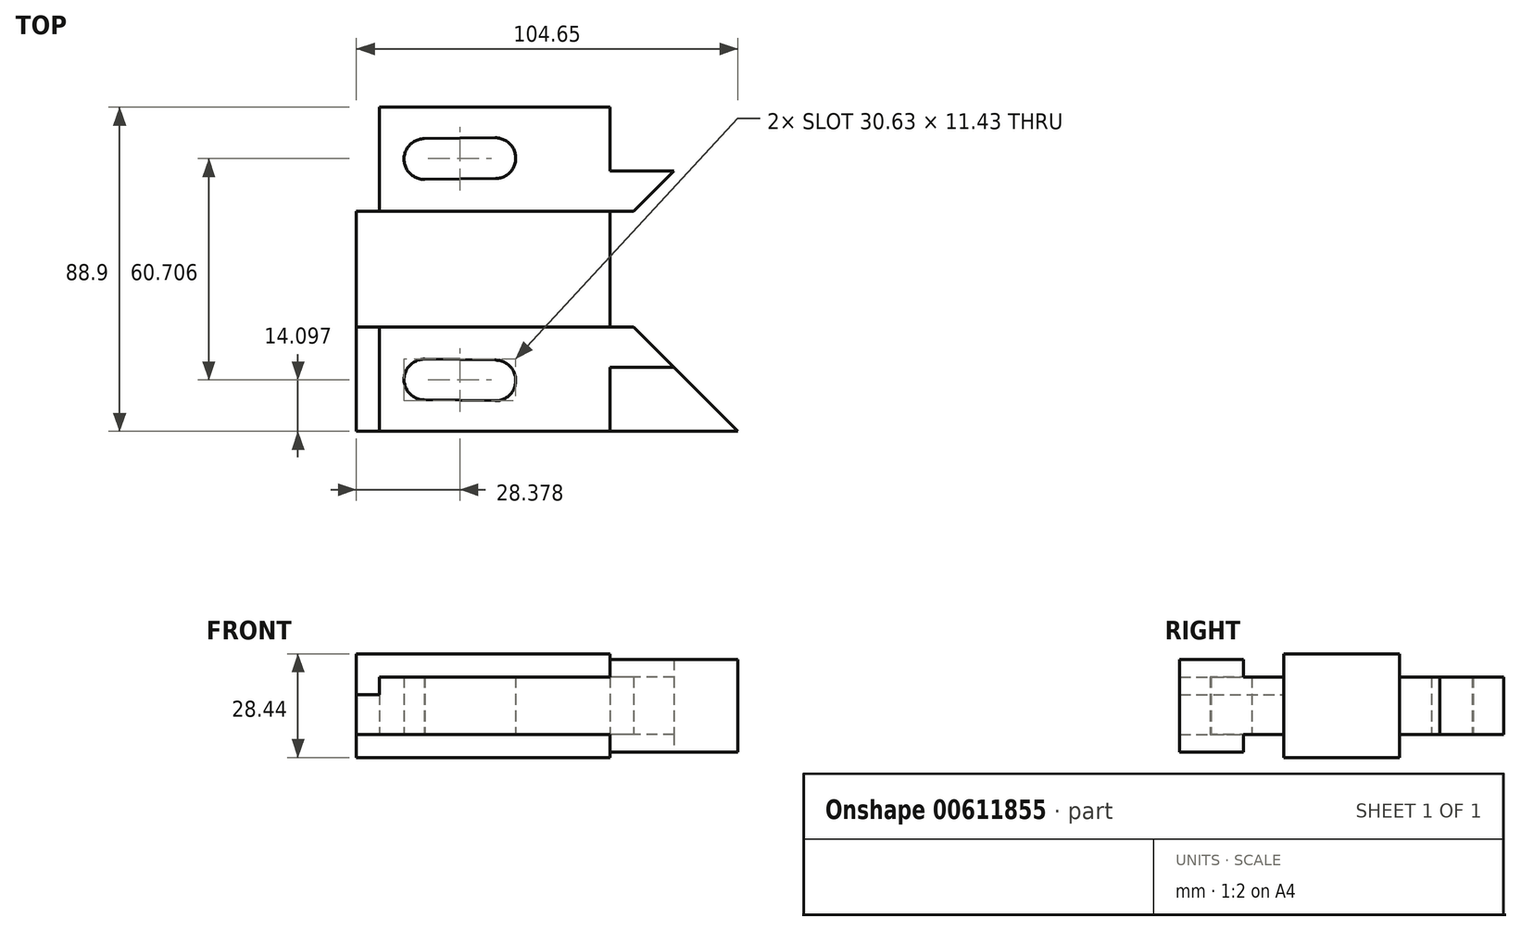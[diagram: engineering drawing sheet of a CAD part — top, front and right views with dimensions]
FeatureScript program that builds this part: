
annotation { "Feature Type Name" : "Feature", "Feature Type Description" : "" }
export const myFeature = defineFeature(function(context is Context, id is Id, definition is map)
    precondition{}
    {
        {
            var Q0;
            Q0=qCreatedBy(makeId("Top.planeOp"),FACE);
            var sketch = newSketch(context, id + "F0", { "sketchPlane" : qUnion([Q0])});
            skLineSegment(sketch, "E0.top", {"start": v(0, 15.88) * mm, "end": v(-69.6, 15.88) * mm});
            skLineSegment(sketch, "E0.left", {"start": v(0, 0) * mm, "end": v(0, 15.88) * mm});
            skLineSegment(sketch, "E0.right", {"start": v(-69.6, 0) * mm, "end": v(-69.6, 15.88) * mm});
            skLineSegment(sketch, "E1.bottom", {"start": v(-69.6, 15.88) * mm, "end": v(-50.95, 15.88) * mm});
            skLineSegment(sketch, "E1.top", {"start": v(-69.6, 44.45) * mm, "end": v(35.05, 44.45) * mm});
            skLineSegment(sketch, "E1.left", {"start": v(-69.6, 15.88) * mm, "end": v(-69.6, 44.45) * mm});
            skLineSegment(sketch, "E2.bottom", {"start": v(-69.6, 44.45) * mm, "end": v(-63.25, 44.45) * mm});
            skLineSegment(sketch, "E2.top", {"start": v(-69.6, 15.88) * mm, "end": v(-63.25, 15.88) * mm});
            skLineSegment(sketch, "E2.left", {"start": v(-69.6, 44.45) * mm, "end": v(-69.6, 15.88) * mm});
            skLineSegment(sketch, "E2.right", {"start": v(-63.25, 44.45) * mm, "end": v(-63.25, 15.88) * mm});
            skLineSegment(sketch, "E3.bottom", {"start": v(35.05, 44.45) * mm, "end": v(0, 44.45) * mm});
            skLineSegment(sketch, "E3.top", {"start": v(17.53, 26.92) * mm, "end": v(0, 26.92) * mm});
            skLineSegment(sketch, "E3.right", {"start": v(0, 44.45) * mm, "end": v(0, 26.92) * mm});
            skLineSegment(sketch, "E4", {"start": v(35.05, 44.45) * mm, "end": v(6.48, 15.88) * mm});
            skPoint(sketch, "E5.MirrorCS.end.orphan", {"position": v(0, -26.92) * mm});
            skPoint(sketch, "E5.MirrorCS.start.orphan", {"position": v(17.53, -26.92) * mm});
            skPoint(sketch, "E6.MirrorCS.start.orphan", {"position": v(0, -44.45) * mm});
            skPoint(sketch, "E7.orphan", {"position": v(35.05, -44.45) * mm});
            skPoint(sketch, "E8.orphan", {"position": v(6.48, -15.88) * mm});
            skPoint(sketch, "E9.MirrorCS.start.orphan", {"position": v(-63.25, -44.45) * mm});
            skPoint(sketch, "E10.MirrorCS.start.orphan", {"position": v(-69.6, -15.88) * mm});
            skPoint(sketch, "E11.MirrorCS.start.orphan", {"position": v(-69.6, -44.45) * mm});
            skPoint(sketch, "E12.MirrorCS.end.orphan", {"position": v(-63.25, -15.88) * mm});
            skPoint(sketch, "E13.MirrorCS.end.orphan", {"position": v(0, -15.88) * mm});
            skPoint(sketch, "E13.MirrorCS.start.orphan", {"position": v(0, 0) * mm});
            skPoint(sketch, "E14.MirrorCS.start.orphan", {"position": v(-69.6, 0) * mm});
            skArc(sketch, "E15", {"start": v(-50.95, 35.81) * mm, "mid": v(-56.54, 30.15) * mm, "end": v(-50.8, 24.64) * mm});
            skArc(sketch, "E16", {"start": v(-31.42, 24.9) * mm, "mid": v(-25.9, 30.55) * mm, "end": v(-31.57, 36.07) * mm});
            skLineSegment(sketch, "E17", {"start": v(-50.95, 35.81) * mm, "end": v(-31.5, 36.07) * mm});
            skLineSegment(sketch, "E18", {"start": v(-50.95, 24.64) * mm, "end": v(-31.42, 24.9) * mm});
            skPoint(sketch, "E19.orphan", {"position": v(-31.5, 15.88) * mm});
            skPoint(sketch, "E20.end.orphan", {"position": v(-50.95, 15.88) * mm});
            skLineSegment(sketch, "E21.trimOffspring", {"start": v(-31.5, 15.88) * mm, "end": v(6.48, 15.88) * mm});
            skLineSegment(sketch, "E22.MirrorCS", {"start": v(-69.6, -44.45) * mm, "end": v(-69.6, -15.88) * mm});
            skLineSegment(sketch, "E23.MirrorCS", {"start": v(-69.6, -44.45) * mm, "end": v(-63.25, -44.45) * mm});
            skLineSegment(sketch, "E24.MirrorCS", {"start": v(-50.95, -35.81) * mm, "end": v(-31.5, -36.07) * mm});
            skPoint(sketch, "E25.MirrorP", {"position": v(-50.95, -15.88) * mm});
            skPoint(sketch, "E26.MirrorP", {"position": v(-31.5, -15.88) * mm});
            skLineSegment(sketch, "E27.MirrorCS", {"start": v(-50.95, -24.64) * mm, "end": v(-31.42, -24.9) * mm});
            skArc(sketch, "E28.MirrorCS", {"start": v(-31.42, -24.9) * mm, "mid": v(-25.9, -30.55) * mm, "end": v(-31.57, -36.07) * mm});
            skArc(sketch, "E29.MirrorCS", {"start": v(-50.95, -35.81) * mm, "mid": v(-56.54, -30.15) * mm, "end": v(-50.8, -24.64) * mm});
            skLineSegment(sketch, "E30.MirrorCS", {"start": v(0, -44.45) * mm, "end": v(0, -26.92) * mm});
            skLineSegment(sketch, "E31.MirrorCS", {"start": v(17.53, -26.92) * mm, "end": v(0, -26.92) * mm});
            skLineSegment(sketch, "E32.MirrorCS", {"start": v(-31.5, -15.88) * mm, "end": v(6.48, -15.88) * mm});
            skLineSegment(sketch, "E33.MirrorCS", {"start": v(0, 0) * mm, "end": v(0, -15.88) * mm});
            skLineSegment(sketch, "E34.MirrorCS", {"start": v(-69.6, -15.88) * mm, "end": v(-69.6, -44.45) * mm});
            skLineSegment(sketch, "E35.MirrorCS", {"start": v(-63.25, -44.45) * mm, "end": v(-63.25, -15.88) * mm});
            skLineSegment(sketch, "E36.MirrorCS", {"start": v(-69.6, -15.88) * mm, "end": v(-63.25, -15.88) * mm});
            skLineSegment(sketch, "E37.MirrorCS", {"start": v(35.05, -44.45) * mm, "end": v(6.48, -15.88) * mm});
            skLineSegment(sketch, "E38.MirrorCS", {"start": v(0, -15.88) * mm, "end": v(-69.6, -15.88) * mm});
            skLineSegment(sketch, "E39.MirrorCS", {"start": v(35.05, -44.45) * mm, "end": v(0, -44.45) * mm});
            skLineSegment(sketch, "E40.MirrorCS", {"start": v(-69.6, -15.88) * mm, "end": v(-50.95, -15.88) * mm});
            skLineSegment(sketch, "E41.MirrorCS", {"start": v(-69.6, -44.45) * mm, "end": v(35.05, -44.45) * mm});
            skLineSegment(sketch, "E42.MirrorCS", {"start": v(-69.6, 0) * mm, "end": v(-69.6, -15.88) * mm});
            skSolve(sketch);
        }
        {
            var Q0;
            {var subQ1=sQuery(id+"F0.wireOp",EDGE,"E0.top");Q0=makeQuery(id+"F0.imprint","IMPRINT",FACE,{"disambiguationData":[TD([[makeQuery(id+"F0.imprint","IMPRINT",EDGE,{"derivedFrom":subQ1}),1.0]])]});}
            extrude(context, id + "F1", {"entities" : qUnion([Q0]), "endBound" : BoundingType.SYMMETRIC, "depth" : 28.45 * mm, "offsetDistance" : 25.4 * mm});
        }
        {
            var Q0;
            {var subQ5=sQuery(id+"F0.wireOp",EDGE,"E0.top");Q0=makeQuery(id+"F0.imprint","IMPRINT",FACE,{"disambiguationData":[TD([[makeQuery(id+"F0.imprint","IMPRINT",EDGE,{"derivedFrom":subQ5}),-1.0]])]});}
            var Q1;
            {var subQ9=sQuery(id+"F0.wireOp",EDGE,"E31.MirrorCS");Q1=makeQuery(id+"F0.imprint","IMPRINT",FACE,{"disambiguationData":[TD([[makeQuery(id+"F0.imprint","IMPRINT",EDGE,{"derivedFrom":subQ9}),-1.0]])]});}
            extrude(context, id + "F2", {"entities" : qUnion([Q0, Q1]), "operationType" : NewBodyOperationType.ADD, "endBound" : BoundingType.SYMMETRIC, "depth" : 15.75 * mm, "offsetDistance" : 25.4 * mm});
        }
        {
            var Q0;
            {var subQ0=sQuery(id+"F0.wireOp",EDGE,"E3.bottom");Q0=makeQuery(id+"F0.imprint","IMPRINT",FACE,{"disambiguationData":[TD([[makeQuery(id+"F0.imprint","IMPRINT",EDGE,{"derivedFrom":subQ0}),1.0]])]});}
            var Q1;
            {var subQ0=sQuery(id+"F0.wireOp",EDGE,"E31.MirrorCS");Q1=makeQuery(id+"F0.imprint","IMPRINT",FACE,{"disambiguationData":[TD([[makeQuery(id+"F0.imprint","IMPRINT",EDGE,{"derivedFrom":subQ0}),1.0]])]});}
            extrude(context, id + "F3", {"entities" : qUnion([Q0, Q1]), "operationType" : NewBodyOperationType.ADD, "endBound" : BoundingType.SYMMETRIC, "depth" : 25.4 * mm, "offsetDistance" : 25.4 * mm});
        }
        {
            var Q0;
            Q0=makeQuery(id+"F0.imprint","IMPRINT",FACE,{"disambiguationData":[TD([[makeQuery(id+"F0.imprint","IMPRINT",EDGE,{"derivedFrom":sQuery(id+"F0.wireOp",EDGE,"E2.bottom")}),-1.0]])]});
            var Q1;
            {var subQ0=sQuery(id+"F0.wireOp",EDGE,"E35.MirrorCS");Q1=makeQuery(id+"F0.imprint","IMPRINT",FACE,{"disambiguationData":[TD([[makeQuery(id+"F0.imprint","IMPRINT",EDGE,{"derivedFrom":subQ0}),1.0]])]});}
            extrude(context, id + "F4", {"entities" : qUnion([Q0, Q1]), "operationType" : NewBodyOperationType.ADD, "depth" : 3.05 * mm, "offsetDistance" : 25.4 * mm, "hasSecondDirection" : true, "secondDirectionOppositeDirection" : true, "secondDirectionDepth" : 7.87 * mm});
        }
    });
